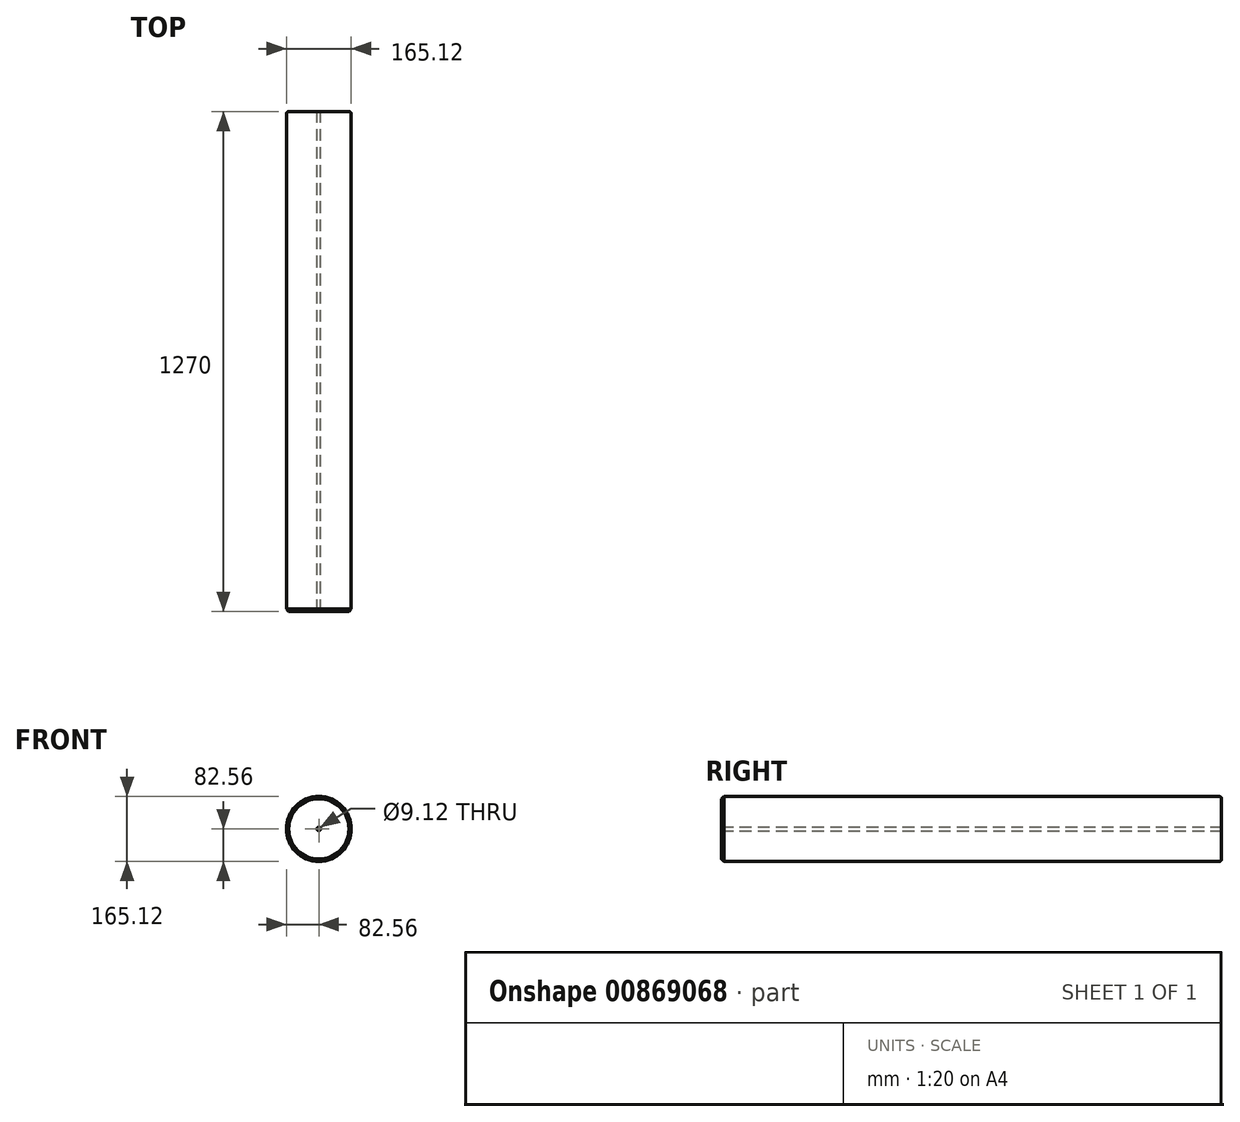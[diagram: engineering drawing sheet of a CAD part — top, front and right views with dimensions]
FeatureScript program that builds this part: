
annotation { "Feature Type Name" : "Feature", "Feature Type Description" : "" }
export const myFeature = defineFeature(function(context is Context, id is Id, definition is map)
    precondition{}
    {
        {
            var Q0;
            Q0=qCreatedBy(makeId("Front.planeOp"),FACE);
            var sketch = newSketch(context, id + "F0", { "sketchPlane" : qUnion([Q0])});
            skCircle(sketch, "E0", {"center": v(0, 0) * mm, "radius": 4.56 * mm});
            skCircle(sketch, "E1", {"center": v(0, 0) * mm, "radius": 82.56 * mm});
            skSolve(sketch);
        }
        {
            var Q0;
            Q0=makeQuery(id+"F0.imprint","IMPRINT",FACE,{"disambiguationData":[TD([[makeQuery(id+"F0.imprint","IMPRINT",EDGE,{"derivedFrom":sQuery(id+"F0.wireOp",EDGE,"E0")}),-1.0]])]});
            extrude(context, id + "F1", {"entities" : qUnion([Q0]), "endBound" : BoundingType.SYMMETRIC, "depth" : 1270 * mm, "offsetDistance" : 25.4 * mm});
        }
        {
            var Q0;
            Q0=makeQuery(id+"F1.opExtrude","CAP_FACE",FACE,{"disambiguationData":[OSD([sQuery(id+"F0.wireOp",EDGE,"E0"),sQuery(id+"F0.wireOp",EDGE,"E1")])],"isStart":true});
            fillet(context, id + "F2", {"entities" : qUnion([Q0]), "radius" : 6 * mm, "tangentPropagation" : true, "allowEdgeOverflow" : false});
        }
        {
            var Q0;
            Q0=makeQuery(id+"F1.opExtrude","CAP_EDGE",EDGE,{"disambiguationData":[OSD([sQuery(id+"F0.wireOp",EDGE,"E1")])],"isStart":false});
            chamfer(context, id + "F3", {"entities" : qUnion([Q0]), "width" : 6 * mm, "tangentPropagation" : true});
        }
    });
